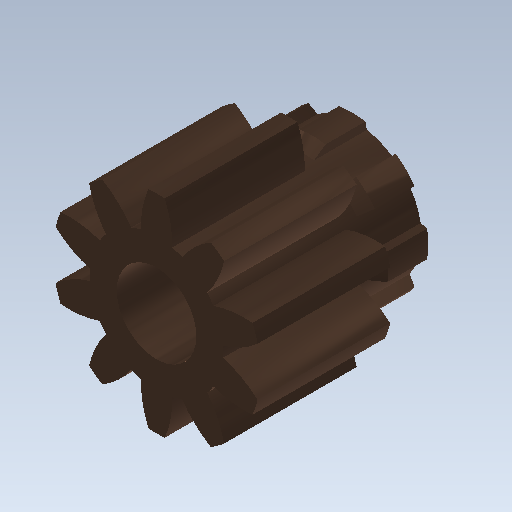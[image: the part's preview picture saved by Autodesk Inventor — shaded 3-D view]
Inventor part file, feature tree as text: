
AUTODESK INVENTOR PART (.ipt)
format: ipt  version: 2020 (Build 240168000, 168)  size: 272,896 bytes
history: native  units: mm (DEFAULTED — no unit token found)
features: sketch x5, extrude x4, plane x3, other x3, chamfer x2, pattern_circular x1
ambient origin geometry x8: Origin, YZ Plane, XZ Plane, XY Plane, X Axis, Y Axis, Z Axis, Center Point
bodies: Solid1 (feature_tree)
feature tree (18):
  extrude  "Extrusion1"  Depth=2.0mm TaperAngle=0.0deg
  plane  "Work Plane2"
  plane  "Work Plane8"
  plane  "Work Plane9"
  other  "Цилиндрическое зубчатое зацепление"
  extrude  "Выдавливание2"  Depth=10.0mm TaperAngle=0.0deg
  extrude  "Выдавливание3"  Depth=2.0mm
  chamfer  "Фаска1"  Distance=3.141593mm
  chamfer  "Фаска2"  [1 undecoded]
  pattern_circular  "Круговой массив1"  [2 undecoded]
  extrude  "Выдавливание4"  Depth=2.0mm
  sketch  "Sketch1"  dims[d0=3.135mm d1=2.0mm d2=0.0mm]
  sketch  "Sketch2"  dims[d3=2.5mm d4=10.0mm d5=0.0mm d16=6.0mm d17=0.0mm d34=3.141593mm d39=0.0mm d41=0.0mm d43=6.0mm d46=6.0mm d47=0.0mm d48=0.0mm d49=2.0mm d50=1.0mm d51=0.0mm d52=0.15mm d53=3.490659mm d54=0.8mm d55=0.0mm d56=0.15mm d57=2.0mm d58=45.0deg d59=0.15mm d60=0.05mm d61=45.0deg d62=80.0mm d63=360.0deg d65=1.2mm d66=5.2mm d67=0.0mm]
  other  "Srf1"
  sketch  "Эскиз3"
  sketch  "Эскиз4"
  sketch  "Эскиз5"
  other  "Средний диаметр"
note: 3 required parameter values undecoded (feature->parameter linkage not recoverable at this tier; creation-order binding heuristic only, values carry confidence <= 0.55)
